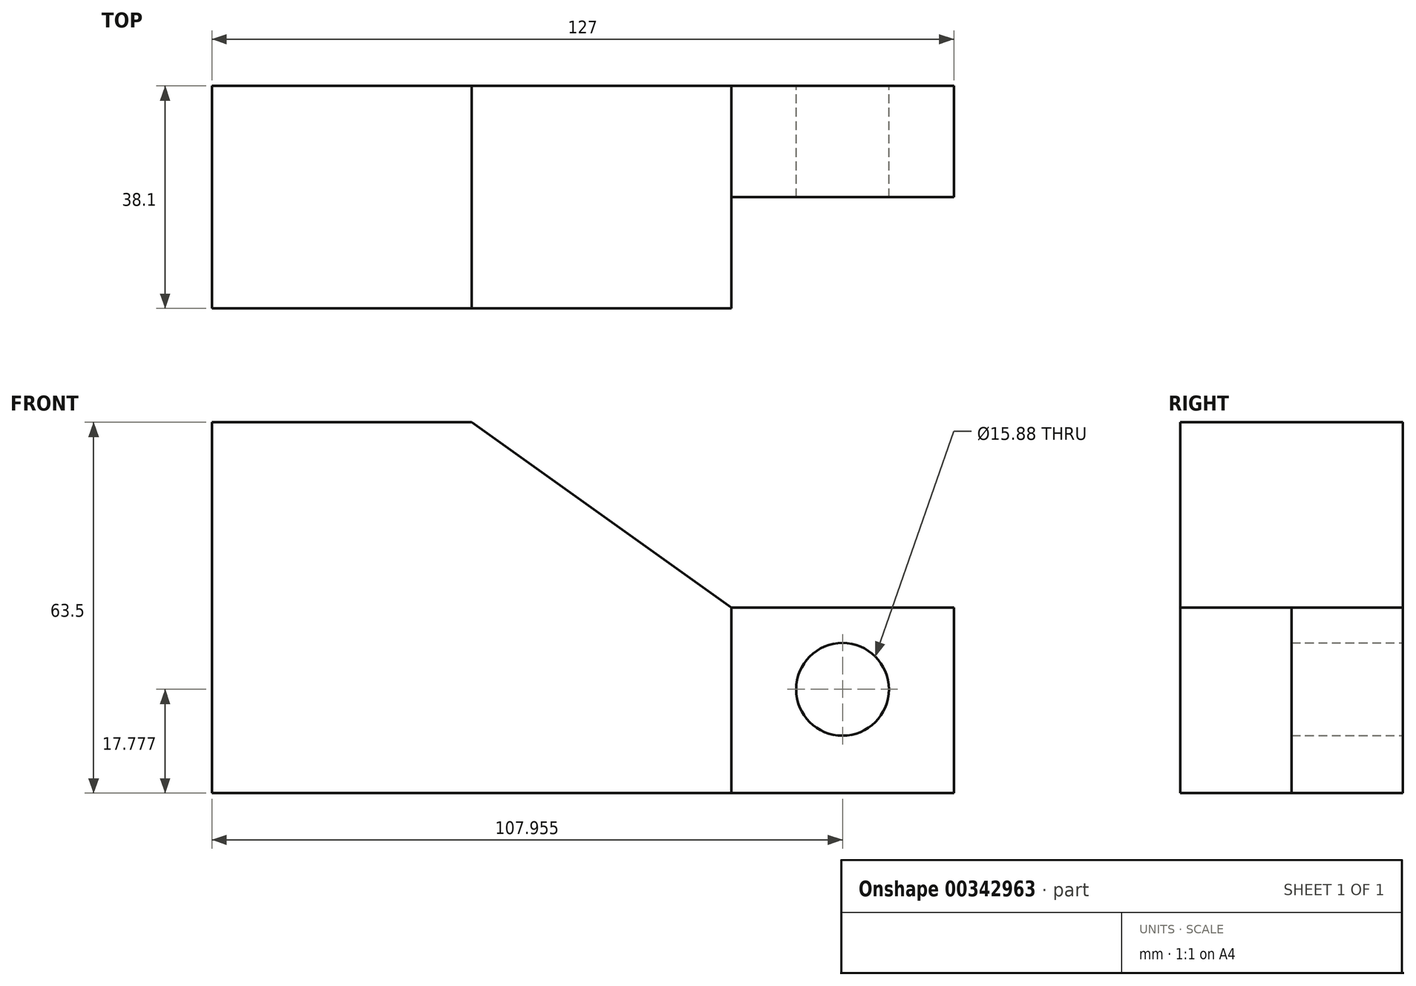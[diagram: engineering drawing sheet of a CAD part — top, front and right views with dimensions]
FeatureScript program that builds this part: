
annotation { "Feature Type Name" : "Feature", "Feature Type Description" : "" }
export const myFeature = defineFeature(function(context is Context, id is Id, definition is map)
    precondition{}
    {
        {
            var Q0;
            Q0=qCreatedBy(makeId("Front.planeOp"),FACE);
            var sketch = newSketch(context, id + "F0", { "sketchPlane" : qUnion([Q0])});
            skLineSegment(sketch, "E0", {"start": v(-70.5, -45.03) * mm, "end": v(56.5, -45.03) * mm});
            skLineSegment(sketch, "E1", {"start": v(-70.5, 18.47) * mm, "end": v(-70.5, -45.03) * mm});
            skLineSegment(sketch, "E2", {"start": v(56.5, -45.03) * mm, "end": v(56.5, -13.28) * mm});
            skLineSegment(sketch, "E3", {"start": v(-70.5, 18.47) * mm, "end": v(-26.05, 18.47) * mm});
            skLineSegment(sketch, "E4", {"start": v(56.5, -13.28) * mm, "end": v(37.45, -13.28) * mm});
            skLineSegment(sketch, "E5", {"start": v(37.45, -13.28) * mm, "end": v(18.4, -13.28) * mm});
            skLineSegment(sketch, "E6", {"start": v(-26.05, 18.47) * mm, "end": v(18.4, -13.28) * mm});
            skCircle(sketch, "E7", {"center": v(37.45, -27.25) * mm, "radius": 7.94 * mm});
            skLineSegment(sketch, "E8", {"start": v(18.4, -13.28) * mm, "end": v(18.4, -45.03) * mm});
            skSolve(sketch);
        }
        {
            var Q0;
            {var subQ0=sQuery(id+"F0.wireOp",EDGE,"E1");Q0=makeQuery(id+"F0.imprint","IMPRINT",FACE,{"disambiguationData":[TD([[makeQuery(id+"F0.imprint","IMPRINT",EDGE,{"derivedFrom":subQ0}),1.0]])]});}
            extrude(context, id + "F1", {"entities" : qUnion([Q0]), "depth" : 38.1 * mm});
        }
        {
            var Q0;
            {var subQ0=sQuery(id+"F0.wireOp",EDGE,"E2");Q0=makeQuery(id+"F0.imprint","IMPRINT",FACE,{"disambiguationData":[TD([[makeQuery(id+"F0.imprint","IMPRINT",EDGE,{"derivedFrom":subQ0}),1.0]])]});}
            extrude(context, id + "F2", {"entities" : qUnion([Q0]), "operationType" : NewBodyOperationType.ADD, "depth" : 19.05 * mm});
        }
    });
